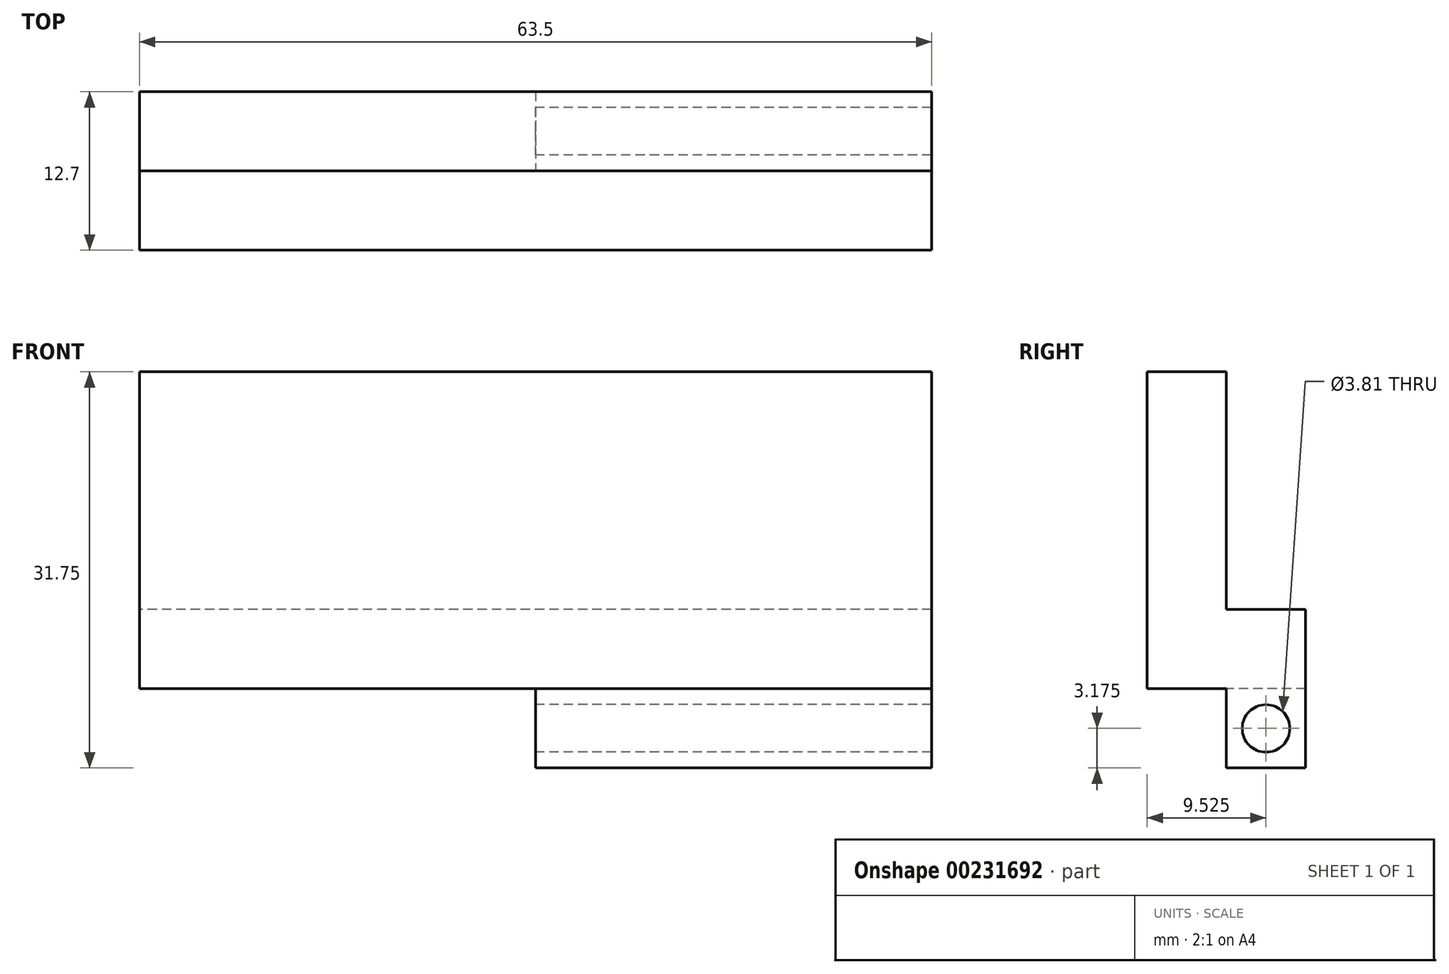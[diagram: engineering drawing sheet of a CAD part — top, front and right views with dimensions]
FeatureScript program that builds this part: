
annotation { "Feature Type Name" : "Feature", "Feature Type Description" : "" }
export const myFeature = defineFeature(function(context is Context, id is Id, definition is map)
    precondition{}
    {
        {
            var Q0;
            Q0=qCreatedBy(makeId("Front.planeOp"),FACE);
            var sketch = newSketch(context, id + "F0", { "sketchPlane" : qUnion([Q0])});
            skLineSegment(sketch, "E0.bottom", {"start": v(0, 0) * mm, "end": v(-63.5, 0) * mm});
            skLineSegment(sketch, "E0.top", {"start": v(0, 25.4) * mm, "end": v(-63.5, 25.4) * mm});
            skLineSegment(sketch, "E0.left", {"start": v(0, 0) * mm, "end": v(0, 25.4) * mm});
            skLineSegment(sketch, "E0.right", {"start": v(-63.5, 0) * mm, "end": v(-63.5, 25.4) * mm});
            skSolve(sketch);
        }
        {
            var Q0;
            Q0=makeQuery(id+"F0.imprint","IMPRINT",FACE,{"disambiguationData":[TD([[makeQuery(id+"F0.imprint","IMPRINT",EDGE,{"derivedFrom":sQuery(id+"F0.wireOp",EDGE,"E0.bottom")}),-1.0]])]});
            extrude(context, id + "F1", {"entities" : qUnion([Q0]), "depth" : 6.35 * mm});
        }
        {
            var Q0;
            Q0=qCreatedBy(makeId("Front.planeOp"),FACE);
            var sketch = newSketch(context, id + "F2", { "sketchPlane" : qUnion([Q0])});
            skLineSegment(sketch, "E1.bottom", {"start": v(0, 0) * mm, "end": v(-63.5, 0) * mm});
            skLineSegment(sketch, "E1.top", {"start": v(0, 6.35) * mm, "end": v(-63.5, 6.35) * mm});
            skLineSegment(sketch, "E1.left", {"start": v(0, 0) * mm, "end": v(0, 6.35) * mm});
            skLineSegment(sketch, "E1.right", {"start": v(-63.5, 0) * mm, "end": v(-63.5, 6.35) * mm});
            skSolve(sketch);
        }
        {
            var Q0;
            Q0=makeQuery(id+"F2.imprint","IMPRINT",FACE,{"disambiguationData":[TD([[makeQuery(id+"F2.imprint","IMPRINT",EDGE,{"derivedFrom":sQuery(id+"F2.wireOp",EDGE,"E1.bottom")}),-1.0]])]});
            extrude(context, id + "F3", {"entities" : qUnion([Q0]), "operationType" : NewBodyOperationType.ADD, "oppositeDirection" : true, "depth" : 6.35 * mm});
        }
        {
            var Q0;
            Q0=makeQuery(id+"F3.boolean.opBoolean","MERGE",FACE,{"derivedFrom":[makeQuery(id+"F1.opExtrude","SWEPT_FACE",FACE,{"disambiguationData":[OSD([sQuery(id+"F0.wireOp",EDGE,"E0.bottom")])]}),makeQuery(id+"F3.opExtrude","SWEPT_FACE",FACE,{"disambiguationData":[OSD([sQuery(id+"F2.wireOp",EDGE,"E1.bottom")])]})]});
            var sketch = newSketch(context, id + "F4", { "sketchPlane" : qUnion([Q0])});
            skLineSegment(sketch, "E2.bottom", {"start": v(0, 0) * mm, "end": v(-63.5, 0) * mm});
            skLineSegment(sketch, "E2.top", {"start": v(0, -6.35) * mm, "end": v(-63.5, -6.35) * mm});
            skLineSegment(sketch, "E2.left", {"start": v(0, 0) * mm, "end": v(0, -6.35) * mm});
            skLineSegment(sketch, "E2.right", {"start": v(-63.5, 0) * mm, "end": v(-63.5, -6.35) * mm});
            skSolve(sketch);
        }
        {
            var Q0;
            Q0=makeQuery(id+"F4.imprint","IMPRINT",FACE,{"disambiguationData":[TD([[makeQuery(id+"F4.imprint","IMPRINT",EDGE,{"derivedFrom":sQuery(id+"F4.wireOp",EDGE,"E2.bottom")}),1.0]])]});
            extrude(context, id + "F5", {"entities" : qUnion([Q0]), "operationType" : NewBodyOperationType.ADD, "depth" : 6.35 * mm});
        }
        {
            var Q0;
            Q0=makeQuery(id+"F5.boolean.opBoolean","MERGE",FACE,{"derivedFrom":[makeQuery(id+"F3.boolean.opBoolean","MERGE",FACE,{"derivedFrom":[makeQuery(id+"F1.opExtrude","SWEPT_FACE",FACE,{"disambiguationData":[OSD([sQuery(id+"F0.wireOp",EDGE,"E0.right")])]}),makeQuery(id+"F3.opExtrude","SWEPT_FACE",FACE,{"disambiguationData":[OSD([sQuery(id+"F2.wireOp",EDGE,"E1.right")])]})]}),makeQuery(id+"F5.opExtrude","SWEPT_FACE",FACE,{"disambiguationData":[OSD([sQuery(id+"F4.wireOp",EDGE,"E2.right")])]})]});
            var sketch = newSketch(context, id + "F6", { "sketchPlane" : qUnion([Q0])});
            skCircle(sketch, "E3", {"center": v(-3.17, -3.17) * mm, "radius": 1.9 * mm});
            skPoint(sketch, "E3.centerSnap0", {"position": v(0, -3.17) * mm});
            skSolve(sketch);
        }
        {
            var Q0;
            Q0=makeQuery(id+"F6.imprint","IMPRINT",FACE,{"disambiguationData":[TD([[makeQuery(id+"F6.imprint","IMPRINT",EDGE,{"derivedFrom":sQuery(id+"F6.wireOp",EDGE,"E3")}),1.0]])]});
            extrude(context, id + "F7", {"entities" : qUnion([Q0]), "operationType" : NewBodyOperationType.REMOVE, "endBound" : BoundingType.THROUGH_ALL, "oppositeDirection" : true, "depth" : 25.4 * mm});
        }
        {
            var Q0;
            Q0=makeQuery(id+"F5.opExtrude","SWEPT_FACE",FACE,{"disambiguationData":[OSD([sQuery(id+"F4.wireOp",EDGE,"E2.bottom")])]});
            var sketch = newSketch(context, id + "F8", { "sketchPlane" : qUnion([Q0])});
            skLineSegment(sketch, "E4.bottom", {"start": v(0, 0) * mm, "end": v(-31.75, 0) * mm});
            skLineSegment(sketch, "E4.top", {"start": v(0, -6.35) * mm, "end": v(-31.75, -6.35) * mm});
            skLineSegment(sketch, "E4.left", {"start": v(0, 0) * mm, "end": v(0, -6.35) * mm});
            skLineSegment(sketch, "E4.right", {"start": v(-31.75, 0) * mm, "end": v(-31.75, -6.35) * mm});
            skSolve(sketch);
        }
        {
            var Q0;
            {var subQ0=sQuery(id+"F8.wireOp",EDGE,"E4.right");Q0=makeQuery(id+"F8.imprint","IMPRINT",FACE,{"disambiguationData":[TD([[makeQuery(id+"F8.imprint","IMPRINT",EDGE,{"derivedFrom":subQ0}),-1.0]])]});}
            extrude(context, id + "F9", {"entities" : qUnion([Q0]), "operationType" : NewBodyOperationType.REMOVE, "oppositeDirection" : true, "depth" : 25.4 * mm});
        }
    });
